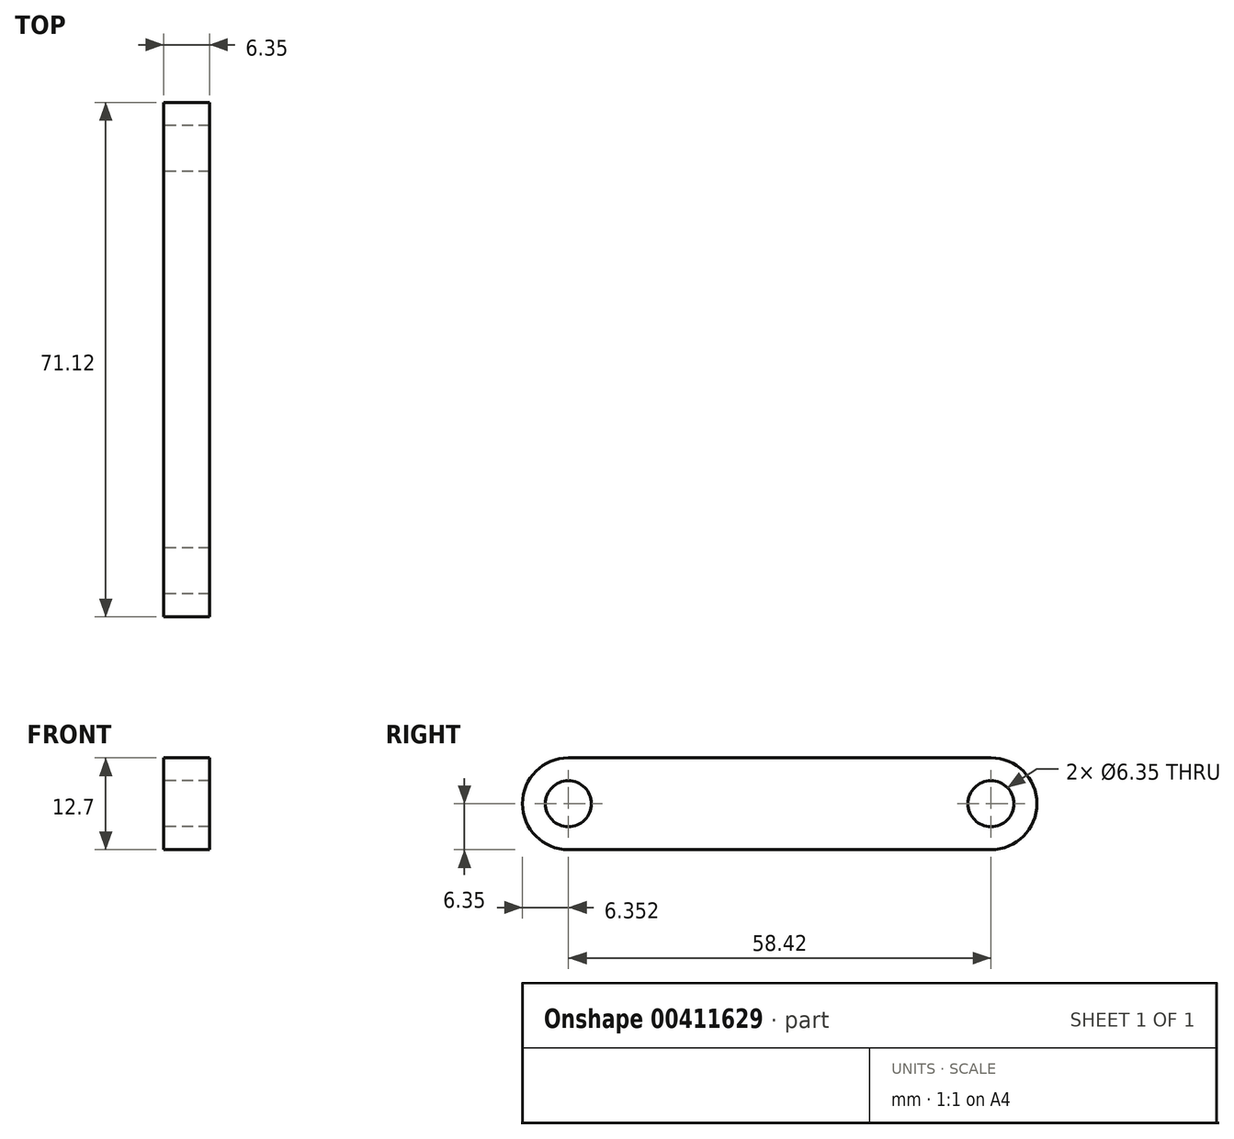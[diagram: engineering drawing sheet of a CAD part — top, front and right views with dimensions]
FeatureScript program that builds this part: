
annotation { "Feature Type Name" : "Feature", "Feature Type Description" : "" }
export const myFeature = defineFeature(function(context is Context, id is Id, definition is map)
    precondition{}
    {
        {
            var Q0;
            Q0=qCreatedBy(makeId("Right.planeOp"),FACE);
            var sketch = newSketch(context, id + "F0", { "sketchPlane" : qUnion([Q0])});
            skArc(sketch, "E0", {"start": v(-24.64, 6.35) * mm, "mid": v(-30.99, 0) * mm, "end": v(-24.64, -6.35) * mm});
            skArc(sketch, "E1", {"start": v(33.78, -6.35) * mm, "mid": v(40.13, 0) * mm, "end": v(33.78, 6.35) * mm});
            skLineSegment(sketch, "E2", {"start": v(-24.64, 6.35) * mm, "end": v(33.78, 6.35) * mm});
            skLineSegment(sketch, "E3", {"start": v(-24.64, -6.35) * mm, "end": v(33.78, -6.35) * mm});
            skCircle(sketch, "E4", {"center": v(-24.64, 0) * mm, "radius": 3.18 * mm});
            skCircle(sketch, "E5", {"center": v(33.78, 0) * mm, "radius": 3.18 * mm});
            skSolve(sketch);
        }
        {
            var Q0;
            Q0 = qSketchRegion(id + "F0", true);
            extrude(context, id + "F1", {"entities" : qUnion([Q0]), "depth" : 6.35 * mm});
        }
    });
